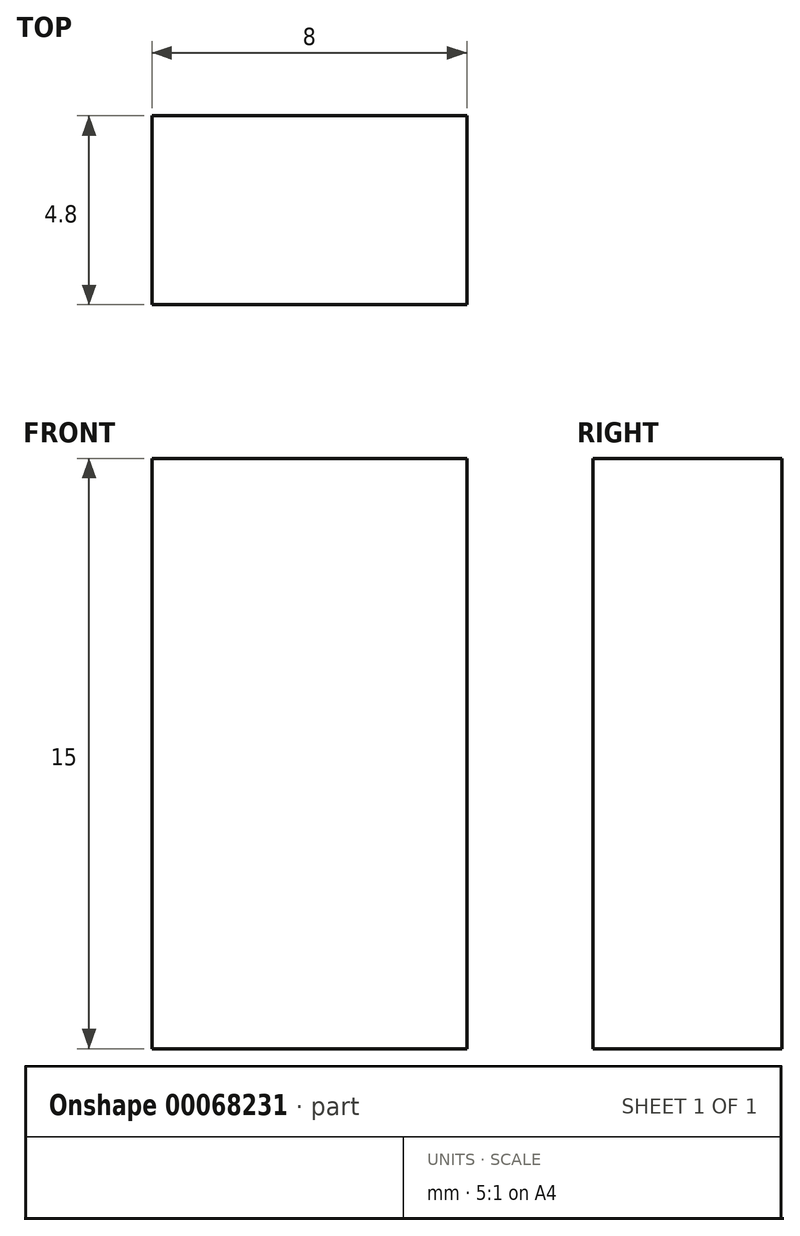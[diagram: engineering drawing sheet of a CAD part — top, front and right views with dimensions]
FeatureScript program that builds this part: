
annotation { "Feature Type Name" : "Feature", "Feature Type Description" : "" }
export const myFeature = defineFeature(function(context is Context, id is Id, definition is map)
    precondition{}
    {
        {
            var Q0;
            Q0=qCreatedBy(makeId("Front.planeOp"),FACE);
            var sketch = newSketch(context, id + "F0", { "sketchPlane" : qUnion([Q0])});
            skLineSegment(sketch, "E0.bottom", {"start": v(-4, 7.5) * mm, "end": v(4, 7.5) * mm});
            skLineSegment(sketch, "E0.top", {"start": v(-4, -7.5) * mm, "end": v(4, -7.5) * mm});
            skLineSegment(sketch, "E0.left", {"start": v(-4, 7.5) * mm, "end": v(-4, -7.5) * mm});
            skLineSegment(sketch, "E0.right", {"start": v(4, 7.5) * mm, "end": v(4, -7.5) * mm});
            skPoint(sketch, "E0.middle", {"position": v(0, 0) * mm});
            skSolve(sketch);
        }
        {
            var Q0;
            Q0=makeQuery(id+"F0.imprint","IMPRINT",FACE,{"disambiguationData":[TD([[makeQuery(id+"F0.imprint","IMPRINT",EDGE,{"derivedFrom":sQuery(id+"F0.wireOp",EDGE,"E0.bottom")}),-1.0]])]});
            extrude(context, id + "F1", {"entities" : qUnion([Q0]), "depth" : 4.8 * mm});
        }
    });
